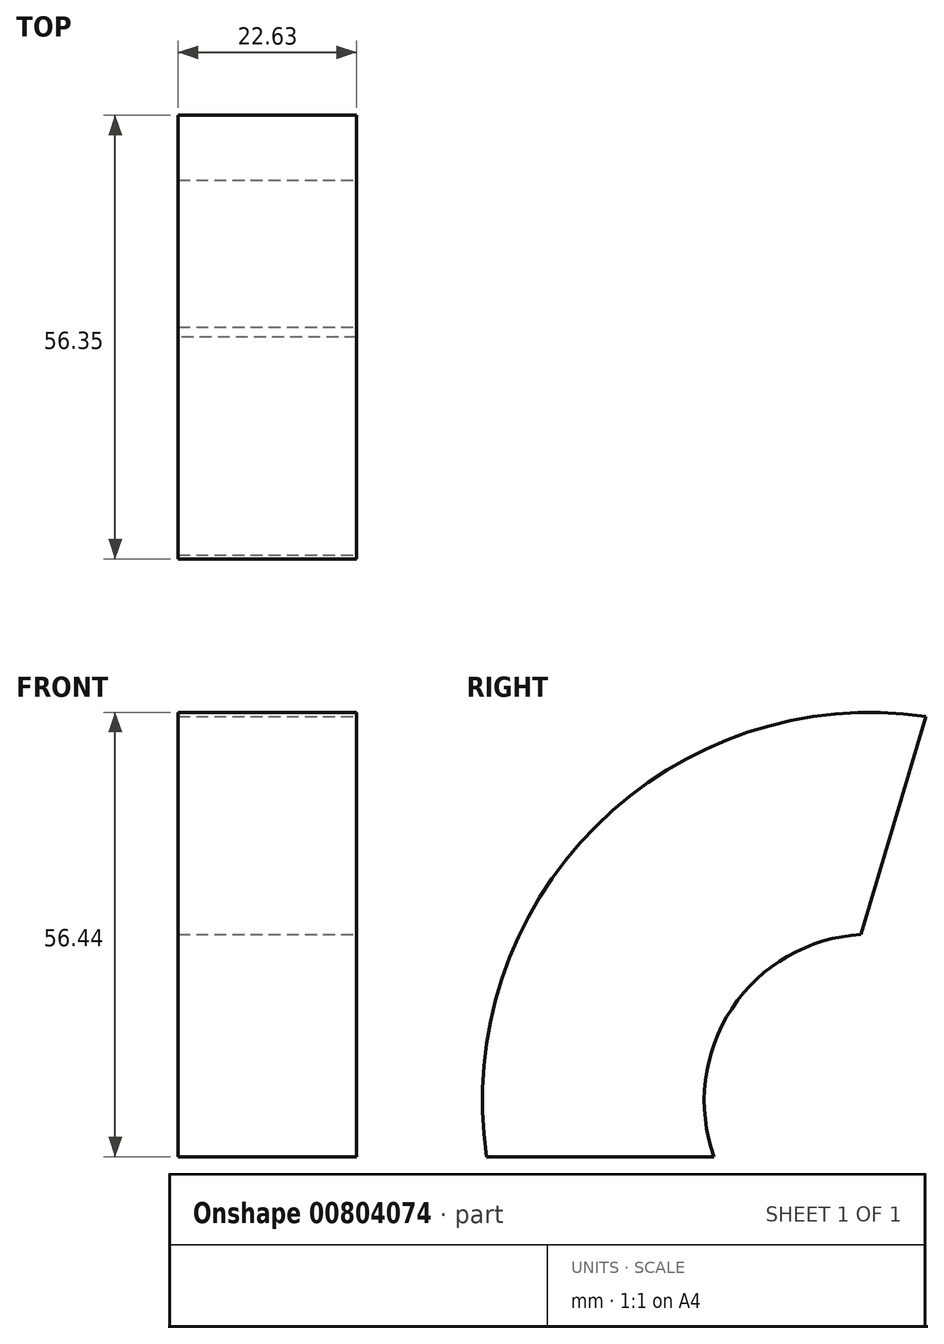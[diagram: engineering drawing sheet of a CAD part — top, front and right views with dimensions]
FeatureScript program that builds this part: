
annotation { "Feature Type Name" : "Feature", "Feature Type Description" : "" }
export const myFeature = defineFeature(function(context is Context, id is Id, definition is map)
    precondition{}
    {
        {
            var Q0;
            Q0=qCreatedBy(makeId("Top.planeOp"),FACE);
            var sketch = newSketch(context, id + "F0", { "sketchPlane" : qUnion([Q0])});
            skLineSegment(sketch, "E0.bottom", {"start": v(0, 0) * mm, "end": v(22.63, 0) * mm});
            skLineSegment(sketch, "E0.top", {"start": v(0, 28.9) * mm, "end": v(22.63, 28.9) * mm});
            skLineSegment(sketch, "E0.left", {"start": v(0, 0) * mm, "end": v(0, 28.9) * mm});
            skLineSegment(sketch, "E0.right", {"start": v(22.63, 0) * mm, "end": v(22.63, 28.9) * mm});
            skSolve(sketch);
        }
        {
            var Q0;
            Q0=qCreatedBy(makeId("Right.planeOp"),FACE);
            var sketch = newSketch(context, id + "F1", { "sketchPlane" : qUnion([Q0])});
            skArc(sketch, "E1", {"start": v(49.59, 34.93) * mm, "mid": v(26.99, 24.4) * mm, "end": v(21.91, 0) * mm});
            skSolve(sketch);
        }
        {
            var Q0;
            Q0=makeQuery(id+"F0.imprint","IMPRINT",FACE,{"disambiguationData":[TD([[makeQuery(id+"F0.imprint","IMPRINT",EDGE,{"derivedFrom":sQuery(id+"F0.wireOp",EDGE,"E0.bottom")}),1.0]])]});
            var Q1;
            Q1=sQuery(id+"F1.wireOp",EDGE,"E1");
            sweep(context, id + "F2", {"profiles" : qUnion([Q0]), "path" : qUnion([Q1])});
        }
    });
